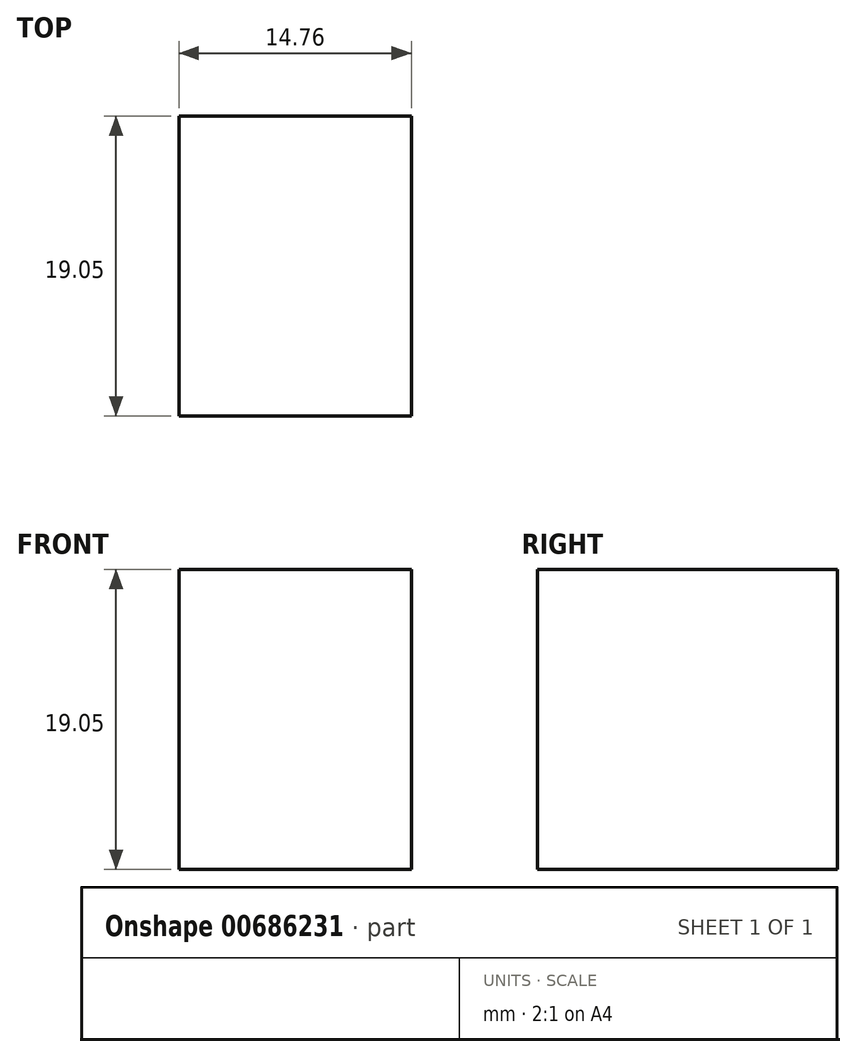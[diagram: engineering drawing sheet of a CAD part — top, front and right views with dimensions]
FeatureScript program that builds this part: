
annotation { "Feature Type Name" : "Feature", "Feature Type Description" : "" }
export const myFeature = defineFeature(function(context is Context, id is Id, definition is map)
    precondition{}
    {
        {
            var Q0;
            Q0=qCreatedBy(makeId("Right.planeOp"),FACE);
            var sketch = newSketch(context, id + "F0", { "sketchPlane" : qUnion([Q0])});
            skLineSegment(sketch, "E0.bottom", {"start": v(0, 0) * mm, "end": v(-19.05, 0) * mm});
            skLineSegment(sketch, "E0.left", {"start": v(0, 0) * mm, "end": v(0, -19.05) * mm});
            skLineSegment(sketch, "E0.right", {"start": v(-19.05, 0) * mm, "end": v(-19.05, -19.05) * mm});
            skLineSegment(sketch, "E1", {"start": v(0, -19.05) * mm, "end": v(-9.53, -19.05) * mm});
            skLineSegment(sketch, "E2", {"start": v(-9.53, -19.05) * mm, "end": v(-19.05, -19.05) * mm});
            skSolve(sketch);
        }
        {
            var Q0;
            Q0 = qSketchRegion(id + "F0", true);
            extrude(context, id + "F1", {"entities" : qUnion([Q0]), "depth" : ((16.25 / 2) - .75) * mm, "offsetDistance" : 25.4 * mm});
        }
        {
            var Q0;
            Q0=makeQuery(id+"F1.opExtrude","SWEPT_BODY",BODY,{"disambiguationData":[OSD([sQuery(id+"F0.wireOp",EDGE,"E0.bottom"),sQuery(id+"F0.wireOp",EDGE,"E0.top"),sQuery(id+"F0.wireOp",EDGE,"E0.left"),sQuery(id+"F0.wireOp",EDGE,"E0.right"),sQuery(id+"F0.wireOp",EDGE,"E1"),sQuery(id+"F0.wireOp",EDGE,"Lk6bxV9J-53qr-2ltE-WDTp-mCcLCdvbsAA5"),sQuery(id+"F0.wireOp",EDGE,"hd399Uyo-XzNY-f011-LtDt-vB2Jmq09eKg8"),sQuery(id+"F0.wireOp",EDGE,"0695be13-852b-4b92-b6cb-74a45e8a9df3.trimOffspring")])]});
            var Q1;
            Q1=qCreatedBy(makeId("Right.planeOp"),FACE);
            mirror(context, id + "F2", {"operationType" : NewBodyOperationType.ADD, "entities" : qUnion([Q0]), "mirrorPlane" : qUnion([Q1])});
        }
    });
